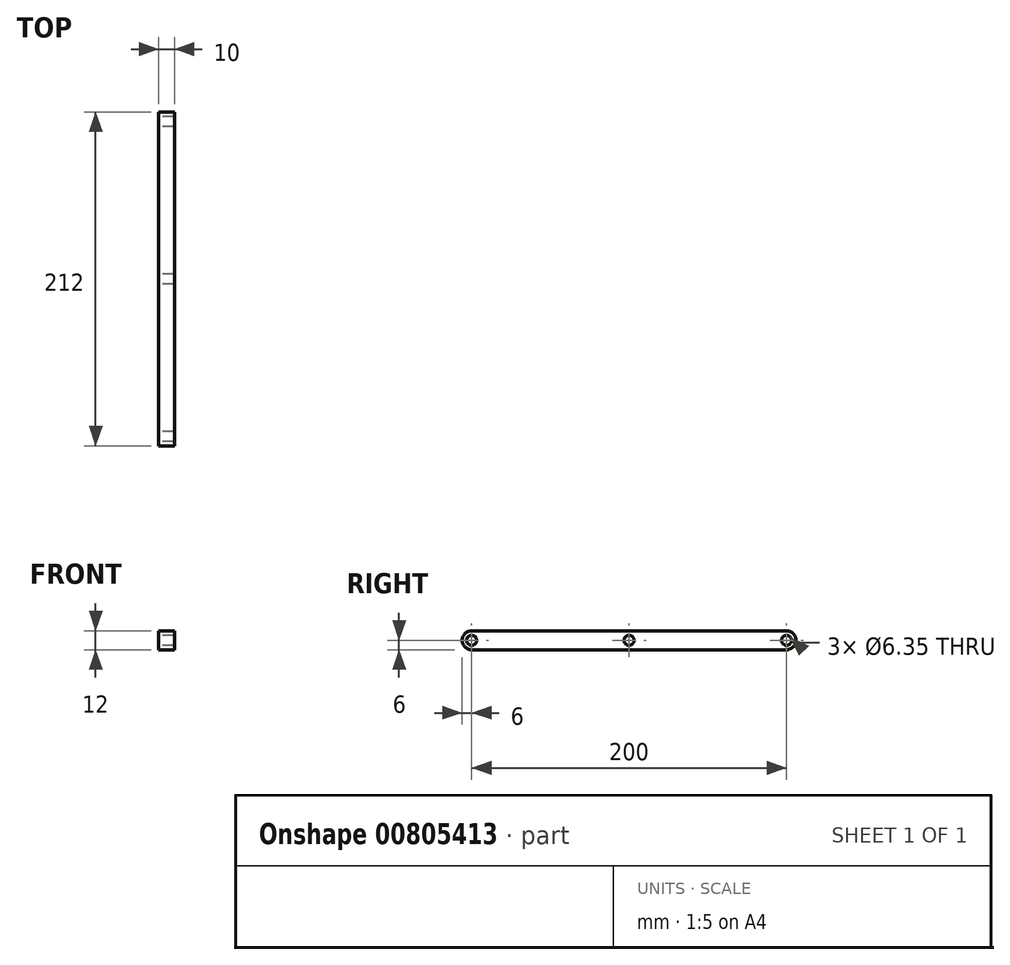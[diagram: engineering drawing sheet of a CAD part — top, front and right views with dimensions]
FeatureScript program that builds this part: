
annotation { "Feature Type Name" : "Feature", "Feature Type Description" : "" }
export const myFeature = defineFeature(function(context is Context, id is Id, definition is map)
    precondition{}
    {
        {
            var Q0;
            Q0=qCreatedBy(makeId("Right.planeOp"),FACE);
            var sketch = newSketch(context, id + "F0", { "sketchPlane" : qUnion([Q0])});
            skLineSegment(sketch, "E0.bottom", {"start": v(-100, 6) * mm, "end": v(100, 6) * mm});
            skLineSegment(sketch, "E0.top", {"start": v(-100, -6) * mm, "end": v(100, -6) * mm});
            skPoint(sketch, "E0.middle", {"position": v(0, 0) * mm});
            skPoint(sketch, "E1", {"position": v(-100, 0) * mm});
            skPoint(sketch, "E2", {"position": v(100, 0) * mm});
            skArc(sketch, "E3", {"start": v(-100, -6) * mm, "mid": v(-106, 0) * mm, "end": v(-100, 6) * mm});
            skArc(sketch, "E4", {"start": v(100, -6) * mm, "mid": v(106, 0) * mm, "end": v(100, 6) * mm});
            skCircle(sketch, "E5", {"center": v(-100, 0) * mm, "radius": 3.17 * mm});
            skCircle(sketch, "E6", {"center": v(0, 0) * mm, "radius": 3.17 * mm});
            skCircle(sketch, "E7", {"center": v(100, 0) * mm, "radius": 3.17 * mm});
            skSolve(sketch);
        }
        {
            var Q0;
            Q0 = qSketchRegion(id + "F0", true);
            extrude(context, id + "F1", {"entities" : qUnion([Q0]), "depth" : 10 * mm, "offsetDistance" : 25 * mm});
        }
    });
